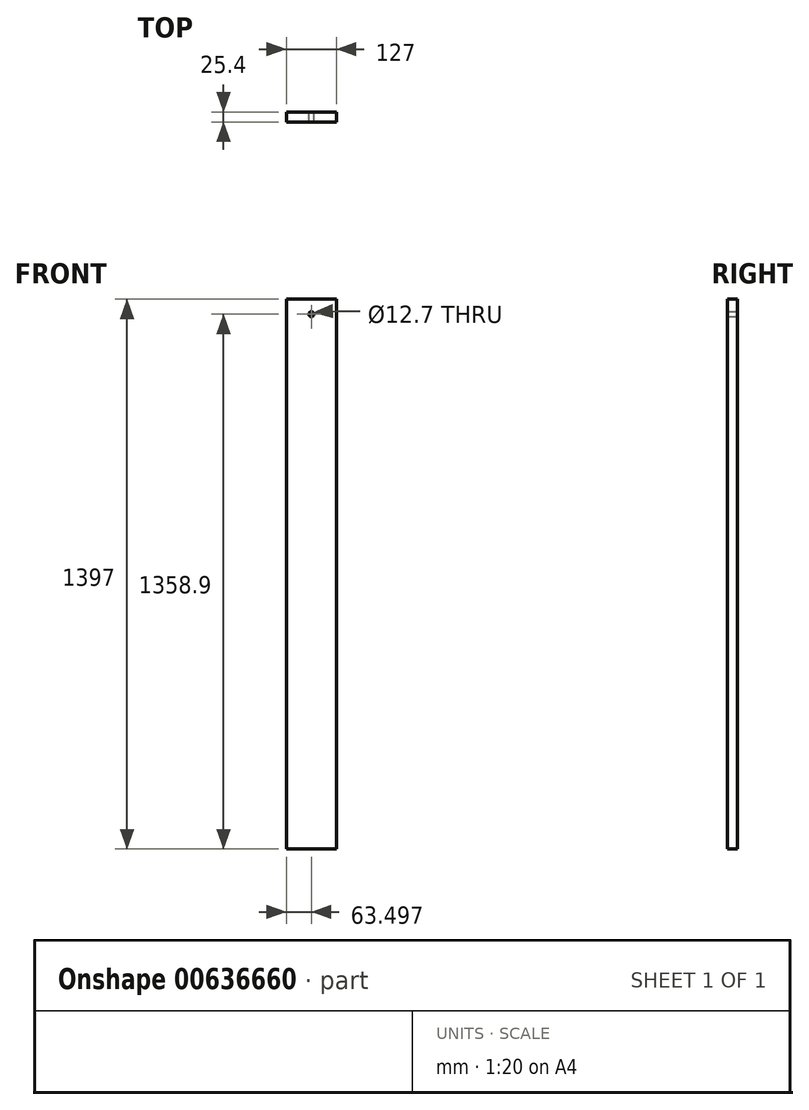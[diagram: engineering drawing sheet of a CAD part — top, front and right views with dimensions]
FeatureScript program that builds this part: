
annotation { "Feature Type Name" : "Feature", "Feature Type Description" : "" }
export const myFeature = defineFeature(function(context is Context, id is Id, definition is map)
    precondition{}
    {
        {
            var Q0;
            Q0=qCreatedBy(makeId("Front.planeOp"),FACE);
            var sketch = newSketch(context, id + "F0", { "sketchPlane" : qUnion([Q0])});
            skLineSegment(sketch, "E0.bottom", {"start": v(-610.7, 866.87) * mm, "end": v(-483.7, 866.87) * mm});
            skLineSegment(sketch, "E0.top", {"start": v(-610.7, -530.13) * mm, "end": v(-483.7, -530.13) * mm});
            skLineSegment(sketch, "E0.left", {"start": v(-610.7, 866.87) * mm, "end": v(-610.7, -530.13) * mm});
            skLineSegment(sketch, "E0.right", {"start": v(-483.7, 866.87) * mm, "end": v(-483.7, -530.13) * mm});
            skLineSegment(sketch, "E1", {"start": v(-547.2, 866.87) * mm, "end": v(-547.2, 828.77) * mm, "construction": true});
            skCircle(sketch, "E2", {"center": v(-547.2, 828.77) * mm, "radius": 6.35 * mm});
            skSolve(sketch);
        }
        {
            var Q0;
            Q0 = qSketchRegion(id + "F0", true);
            extrude(context, id + "F1", {"entities" : qUnion([Q0]), "depth" : 25.4 * mm, "offsetDistance" : 25.4 * mm});
        }
        {
            var Q0;
            Q0=sQuery(id+"F0.wireOp",EDGE,"E2");
            extrude(context, id + "F2", {"bodyType" : ToolBodyType.SURFACE, "surfaceEntities" : qUnion([Q0]), "depth" : 25.4 * mm, "offsetDistance" : 25.4 * mm});
        }
    });
